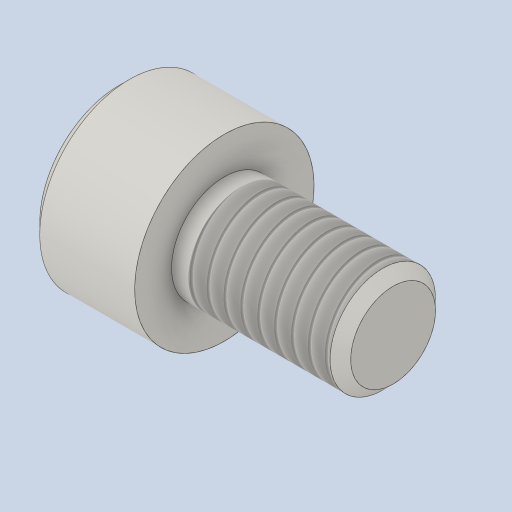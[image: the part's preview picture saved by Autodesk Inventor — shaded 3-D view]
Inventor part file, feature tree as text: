
AUTODESK INVENTOR PART (.ipt)
format: ipt  version: 2023 (Build 270158000, 158)  size: 208,384 bytes
history: native  units: mm
features: other x14, sketch x3, revolve x1, thread x1, hole x1, extrude x1
ambient origin geometry x8: Origin, YZ Plane, XZ Plane, XY Plane, X Axis, Y Axis, Z Axis, Center Point
bodies: Solid1 (feature_tree)
feature tree (21):
  revolve  "Revolution1"  [1 undecoded]
  thread  "Thread1"  [1 undecoded]
  hole  "Hole1"  [1 undecoded]
  extrude  "Extrusion1"  [1 undecoded]
  other  "bolt_XY"
  other  "bolt_YZ"
  other  "bolt_ZX"
  other  "bolt_X"
  other  "bolt_Y"
  other  "bolt_Z"
  other  "bolt_Center"
  other  "nut_XY"
  other  "nut_YZ"
  other  "nut_ZX"
  other  "nut_X"
  other  "nut_Y"
  other  "nut_Z"
  other  "nut_Center"
  sketch  "Sketch_1"  dims[d0=360.0deg d1=6.7095mm d2=0.0mm]
  sketch  "Sketch2"  dims[d3=4.0mm d4=6.0mm d5=4.0mm d6=2.0mm d7=90.0deg d8=2.5mm d9=150.0deg d10=2.5mm d11=0.0mm]
  sketch  "Sketch_3"  dims[d12=0.0mm d13=0.0mm]
note: 4 required parameter values undecoded (feature->parameter linkage not recoverable at this tier; creation-order binding heuristic only, values carry confidence <= 0.55)